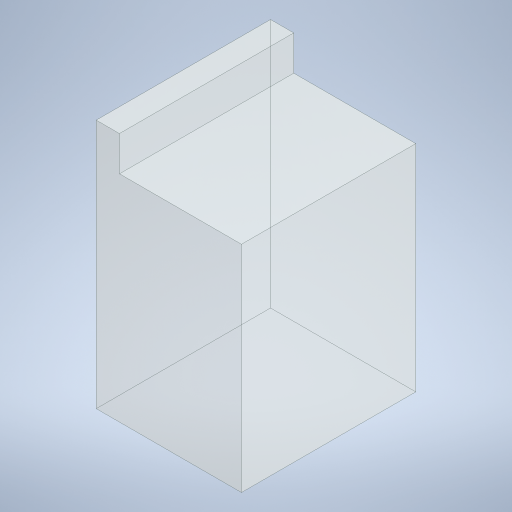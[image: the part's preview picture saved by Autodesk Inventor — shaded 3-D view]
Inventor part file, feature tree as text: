
AUTODESK INVENTOR PART (.ipt)
format: ipt  version: 2024 (Build 280153000, 153)  size: 239,616 bytes
history: native  units: in
note: dims shown in document units (in); Inventor stores cm internally (conversion verified against a paired STEP export)
features: extrude x2, sketch x2
ambient origin geometry x8: Origin, YZ Plane, XZ Plane, XY Plane, X Axis, Y Axis, Z Axis, Center Point
bodies: Solid1 (feature_tree)
feature tree (4):
  extrude  "Extrusion1"  Depth=30.0in
  extrude  "Extrusion2"  Depth=4.0in
  sketch  "Sketch1"  dims[d2=37.0in d3=0.0in d4=30.0in]
  sketch  "Sketch2"  dims[d5=25.0in d6=4.0in d7=6.0in d8=0.0in]
